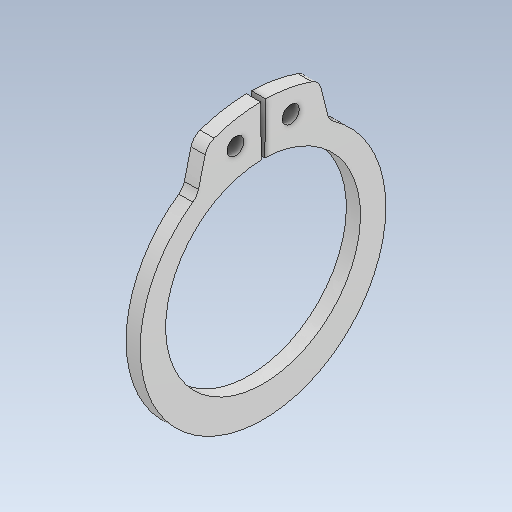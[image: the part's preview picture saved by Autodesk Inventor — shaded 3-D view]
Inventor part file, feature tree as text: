
AUTODESK INVENTOR PART (.ipt)
format: ipt  version: 2020 (Build 240168000, 168)  size: 114,176 bytes
history: native  units: in
note: dims shown in document units (in); Inventor stores cm internally (conversion verified against a paired STEP export)
features: fillet x1
ambient origin geometry x8: Origin, YZ Plane, XZ Plane, XY Plane, X Axis, Y Axis, Z Axis, Center Point
bodies: Solid1 (feature_tree)
feature tree (1):
  fillet  "Fillet1"  [1 undecoded]
note: 1 required parameter value undecoded (feature->parameter linkage not recoverable at this tier; creation-order binding heuristic only, values carry confidence <= 0.55)
